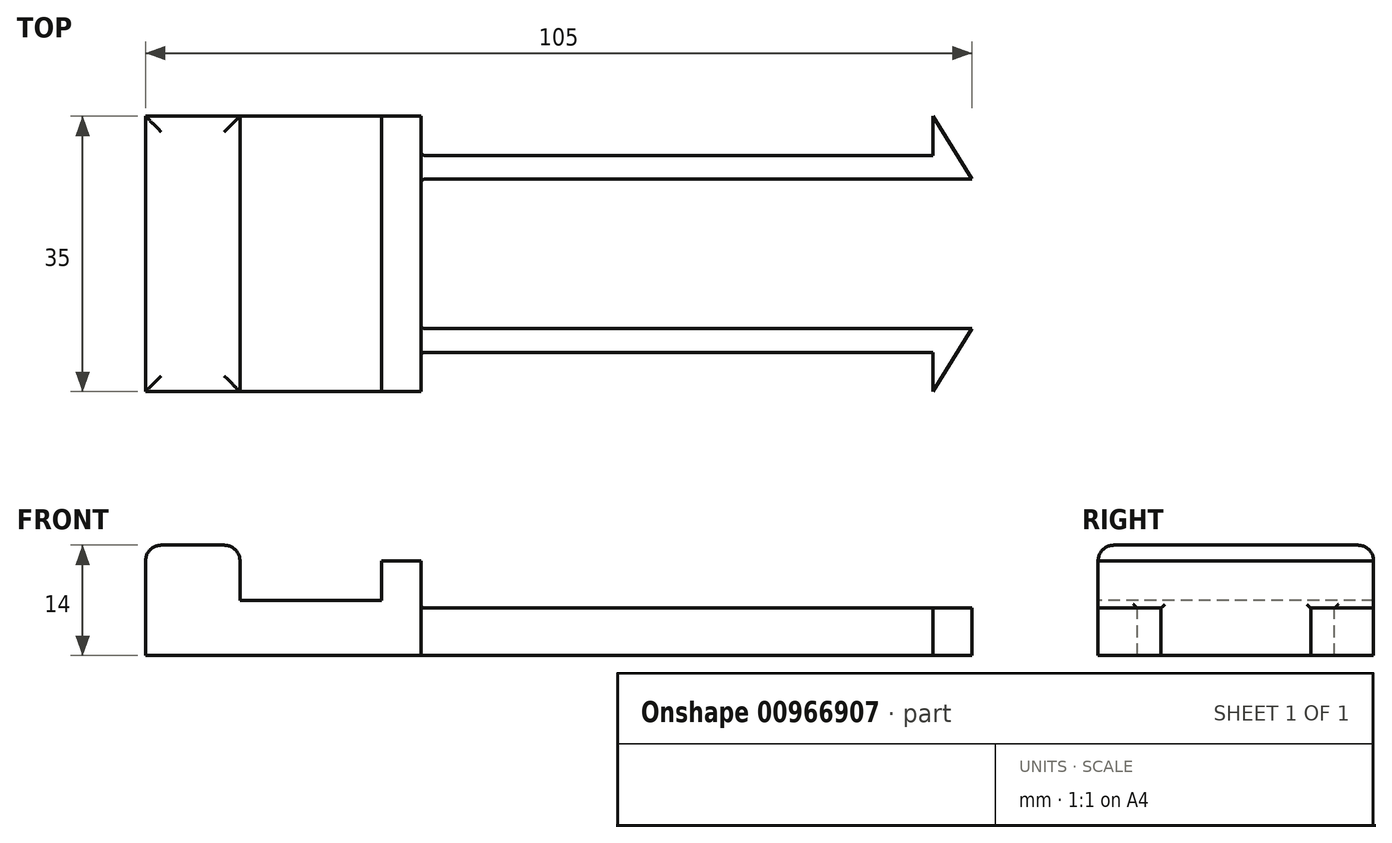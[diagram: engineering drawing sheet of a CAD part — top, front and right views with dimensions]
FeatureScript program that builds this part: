
annotation { "Feature Type Name" : "Feature", "Feature Type Description" : "" }
export const myFeature = defineFeature(function(context is Context, id is Id, definition is map)
    precondition{}
    {
        {
            var Q0;
            Q0=qCreatedBy(makeId("Top.planeOp"),FACE);
            var sketch = newSketch(context, id + "F0", { "sketchPlane" : qUnion([Q0])});
            skLineSegment(sketch, "E0.bottom", {"start": v(52.5, -17.5) * mm, "end": v(-52.5, -17.5) * mm});
            skLineSegment(sketch, "E0.top", {"start": v(52.5, 17.5) * mm, "end": v(-52.5, 17.5) * mm});
            skLineSegment(sketch, "E0.left", {"start": v(52.5, -17.5) * mm, "end": v(52.5, 17.5) * mm});
            skLineSegment(sketch, "E0.right", {"start": v(-52.5, -17.5) * mm, "end": v(-52.5, 17.5) * mm});
            skPoint(sketch, "E0.middle", {"position": v(0, 0) * mm});
            skSolve(sketch);
        }
        {
            var Q0;
            Q0 = qSketchRegion(id + "F0", true);
            extrude(context, id + "F1", {"entities" : qUnion([Q0]), "depth" : 7 * mm, "offsetDistance" : 25 * mm});
        }
        {
            var Q0;
            Q0=makeQuery(id+"F1.opExtrude","CAP_FACE",FACE,{"disambiguationData":[OSD([sQuery(id+"F0.wireOp",EDGE,"E0.bottom"),sQuery(id+"F0.wireOp",EDGE,"E0.top"),sQuery(id+"F0.wireOp",EDGE,"E0.left"),sQuery(id+"F0.wireOp",EDGE,"E0.right")])],"isStart":false});
            var sketch = newSketch(context, id + "F2", { "sketchPlane" : qUnion([Q0])});
            skLineSegment(sketch, "E1", {"start": v(-17.5, 17.5) * mm, "end": v(-17.5, -17.5) * mm});
            skLineSegment(sketch, "E2", {"start": v(-17.5, 9.5) * mm, "end": v(52.5, 9.5) * mm});
            skLineSegment(sketch, "E3", {"start": v(-17.5, -9.5) * mm, "end": v(52.5, -9.5) * mm});
            skSolve(sketch);
        }
        {
            var Q0;
            Q0 = qSketchRegion(id + "F2", true);
            var Q1;
            {var subQ0=sQuery(id+"F2.wireOp",EDGE,"E2");Q1=makeQuery(id+"F2.imprint","IMPRINT",FACE,{"disambiguationData":[TD([[makeQuery(id+"F2.imprint","IMPRINT",EDGE,{"derivedFrom":subQ0}),-1.0]])]});}
            extrude(context, id + "F3", {"entities" : qUnion([Q0, Q1]), "operationType" : NewBodyOperationType.REMOVE, "endBound" : BoundingType.THROUGH_ALL, "oppositeDirection" : true, "depth" : 25 * mm, "offsetDistance" : 25 * mm});
        }
        {
            var Q0;
            Q0=makeQuery(id+"F1.opExtrude","CAP_FACE",FACE,{"disambiguationData":[OSD([sQuery(id+"F0.wireOp",EDGE,"E0.bottom"),sQuery(id+"F0.wireOp",EDGE,"E0.top"),sQuery(id+"F0.wireOp",EDGE,"E0.left"),sQuery(id+"F0.wireOp",EDGE,"E0.right")])],"isStart":false});
            var sketch = newSketch(context, id + "F4", { "sketchPlane" : qUnion([Q0])});
            skLineSegment(sketch, "E4", {"start": v(47.5, 17.5) * mm, "end": v(47.5, -17.5) * mm, "construction": true});
            skLineSegment(sketch, "E5", {"start": v(47.5, 17.5) * mm, "end": v(52.5, 9.5) * mm});
            skSolve(sketch);
        }
        {
            var Q0;
            Q0 = qSketchRegion(id + "F4", true);
            var Q1;
            {var subQ0=sQuery(id+"F4.wireOp",EDGE,"E5");Q1=makeQuery(id+"F4.imprint","IMPRINT",FACE,{"disambiguationData":[TD([[makeQuery(id+"F4.imprint","IMPRINT",EDGE,{"derivedFrom":subQ0}),1.0]])]});}
            extrude(context, id + "F5", {"entities" : qUnion([Q0, Q1]), "operationType" : NewBodyOperationType.REMOVE, "endBound" : BoundingType.THROUGH_ALL, "oppositeDirection" : true, "depth" : 25 * mm, "offsetDistance" : 25 * mm});
        }
        {
            var Q0;
            Q0=makeQuery(id+"F1.opExtrude","CAP_FACE",FACE,{"disambiguationData":[OSD([sQuery(id+"F0.wireOp",EDGE,"E0.bottom"),sQuery(id+"F0.wireOp",EDGE,"E0.top"),sQuery(id+"F0.wireOp",EDGE,"E0.left"),sQuery(id+"F0.wireOp",EDGE,"E0.right")])],"isStart":false});
            var sketch = newSketch(context, id + "F6", { "sketchPlane" : qUnion([Q0])});
            skLineSegment(sketch, "E6", {"start": v(47.5, -9.5) * mm, "end": v(47.5, -17.5) * mm});
            skLineSegment(sketch, "E7", {"start": v(47.5, -17.5) * mm, "end": v(52.5, -9.5) * mm});
            skSolve(sketch);
        }
        {
            var Q0;
            Q0 = qSketchRegion(id + "F6", true);
            var Q1;
            {var subQ0=sQuery(id+"F6.wireOp",EDGE,"E7");Q1=makeQuery(id+"F6.imprint","IMPRINT",FACE,{"disambiguationData":[TD([[makeQuery(id+"F6.imprint","IMPRINT",EDGE,{"derivedFrom":subQ0}),-1.0]])]});}
            extrude(context, id + "F7", {"entities" : qUnion([Q0, Q1]), "operationType" : NewBodyOperationType.REMOVE, "endBound" : BoundingType.THROUGH_ALL, "oppositeDirection" : true, "depth" : 25 * mm, "offsetDistance" : 25 * mm});
        }
        {
            var Q0;
            Q0=makeQuery(id+"F1.opExtrude","CAP_FACE",FACE,{"disambiguationData":[OSD([sQuery(id+"F0.wireOp",EDGE,"E0.bottom"),sQuery(id+"F0.wireOp",EDGE,"E0.top"),sQuery(id+"F0.wireOp",EDGE,"E0.left"),sQuery(id+"F0.wireOp",EDGE,"E0.right")])],"isStart":false});
            var sketch = newSketch(context, id + "F8", { "sketchPlane" : qUnion([Q0])});
            skLineSegment(sketch, "E8", {"start": v(-17.5, 17.5) * mm, "end": v(-17.5, -17.5) * mm, "construction": true});
            skLineSegment(sketch, "E9.bottom", {"start": v(-17.5, 17.5) * mm, "end": v(47.5, 17.5) * mm});
            skLineSegment(sketch, "E9.top", {"start": v(-17.5, 12.5) * mm, "end": v(47.5, 12.5) * mm});
            skLineSegment(sketch, "E9.left", {"start": v(-17.5, 17.5) * mm, "end": v(-17.5, 12.5) * mm});
            skLineSegment(sketch, "E9.right", {"start": v(47.5, 17.5) * mm, "end": v(47.5, 12.5) * mm});
            skSolve(sketch);
        }
        {
            var Q0;
            Q0 = qSketchRegion(id + "F8", true);
            extrude(context, id + "F9", {"entities" : qUnion([Q0]), "operationType" : NewBodyOperationType.REMOVE, "endBound" : BoundingType.THROUGH_ALL, "oppositeDirection" : true, "depth" : 25 * mm, "offsetDistance" : 25 * mm});
        }
        {
            var Q0;
            Q0=makeQuery(id+"F1.opExtrude","CAP_FACE",FACE,{"disambiguationData":[OSD([sQuery(id+"F0.wireOp",EDGE,"E0.bottom"),sQuery(id+"F0.wireOp",EDGE,"E0.top"),sQuery(id+"F0.wireOp",EDGE,"E0.left"),sQuery(id+"F0.wireOp",EDGE,"E0.right")])],"isStart":false});
            var sketch = newSketch(context, id + "F10", { "sketchPlane" : qUnion([Q0])});
            skLineSegment(sketch, "E10", {"start": v(-17.5, 17.5) * mm, "end": v(-17.5, -17.5) * mm, "construction": true});
            skLineSegment(sketch, "E11.bottom", {"start": v(-17.5, -17.5) * mm, "end": v(47.5, -17.5) * mm});
            skLineSegment(sketch, "E11.top", {"start": v(-17.5, -12.5) * mm, "end": v(47.5, -12.5) * mm});
            skLineSegment(sketch, "E11.left", {"start": v(-17.5, -17.5) * mm, "end": v(-17.5, -12.5) * mm});
            skLineSegment(sketch, "E11.right", {"start": v(47.5, -17.5) * mm, "end": v(47.5, -12.5) * mm});
            skSolve(sketch);
        }
        {
            var Q0;
            Q0 = qSketchRegion(id + "F10", true);
            extrude(context, id + "F11", {"entities" : qUnion([Q0]), "operationType" : NewBodyOperationType.REMOVE, "endBound" : BoundingType.THROUGH_ALL, "oppositeDirection" : true, "depth" : 25 * mm, "offsetDistance" : 25 * mm});
        }
        {
            var Q0;
            Q0=makeQuery(id+"F1.opExtrude","CAP_FACE",FACE,{"disambiguationData":[OSD([sQuery(id+"F0.wireOp",EDGE,"E0.bottom"),sQuery(id+"F0.wireOp",EDGE,"E0.top"),sQuery(id+"F0.wireOp",EDGE,"E0.left"),sQuery(id+"F0.wireOp",EDGE,"E0.right")])],"isStart":false});
            var sketch = newSketch(context, id + "F12", { "sketchPlane" : qUnion([Q0])});
            skPoint(sketch, "E12", {"position": v(-22.5, 17.5) * mm});
            skLineSegment(sketch, "E13.bottom", {"start": v(-22.5, 17.5) * mm, "end": v(-17.5, 17.5) * mm});
            skLineSegment(sketch, "E13.top", {"start": v(-22.5, -17.5) * mm, "end": v(-17.5, -17.5) * mm});
            skLineSegment(sketch, "E13.left", {"start": v(-22.5, 17.5) * mm, "end": v(-22.5, -17.5) * mm});
            skLineSegment(sketch, "E13.right", {"start": v(-17.5, 17.5) * mm, "end": v(-17.5, -17.5) * mm});
            skSolve(sketch);
        }
        {
            var Q0;
            Q0 = qSketchRegion(id + "F12", true);
            extrude(context, id + "F13", {"entities" : qUnion([Q0]), "operationType" : NewBodyOperationType.ADD, "depth" : 5 * mm, "offsetDistance" : 25 * mm});
        }
        {
            var Q0;
            {var subQ0=sQuery(id+"F0.wireOp",EDGE,"E0.top");var subQ1=sQuery(id+"F0.wireOp",EDGE,"E0.right");var subQ2=sQuery(id+"F0.wireOp",EDGE,"E0.bottom");Q0=makeQuery(id+"F13.boolean.opBoolean","SPLIT",FACE,{"disambiguationData":[TD([makeQuery(id+"F1.opExtrude","SWEPT_FACE",FACE,{"disambiguationData":[OSD([subQ2])]})])],"derivedFrom":makeQuery(id+"F1.opExtrude","CAP_FACE",FACE,{"disambiguationData":[OSD([subQ2,subQ0,sQuery(id+"F0.wireOp",EDGE,"E0.left"),subQ1])],"isStart":false})});}
            var sketch = newSketch(context, id + "F14", { "sketchPlane" : qUnion([Q0])});
            skLineSegment(sketch, "E14.bottom", {"start": v(-52.5, 17.5) * mm, "end": v(-40.5, 17.5) * mm});
            skLineSegment(sketch, "E14.top", {"start": v(-52.5, -17.5) * mm, "end": v(-40.5, -17.5) * mm});
            skLineSegment(sketch, "E14.left", {"start": v(-52.5, 17.5) * mm, "end": v(-52.5, -17.5) * mm});
            skLineSegment(sketch, "E14.right", {"start": v(-40.5, 17.5) * mm, "end": v(-40.5, -17.5) * mm});
            skSolve(sketch);
        }
        {
            var Q0;
            Q0 = qSketchRegion(id + "F14", true);
            extrude(context, id + "F15", {"entities" : qUnion([Q0]), "operationType" : NewBodyOperationType.ADD, "depth" : 7 * mm, "offsetDistance" : 25 * mm});
        }
        {
            var Q0;
            Q0=makeQuery(id+"F15.opExtrude","CAP_EDGE",EDGE,{"disambiguationData":[OSD([sQuery(id+"F14.wireOp",EDGE,"E14.right")])],"isStart":false});
            var Q1;
            Q1=makeQuery(id+"F15.opExtrude","CAP_EDGE",EDGE,{"disambiguationData":[OSD([sQuery(id+"F14.wireOp",EDGE,"E14.bottom")])],"isStart":false});
            var Q2;
            Q2=makeQuery(id+"F15.opExtrude","CAP_EDGE",EDGE,{"disambiguationData":[OSD([sQuery(id+"F14.wireOp",EDGE,"E14.top")])],"isStart":false});
            var Q3;
            Q3=makeQuery(id+"F15.opExtrude","CAP_EDGE",EDGE,{"disambiguationData":[OSD([sQuery(id+"F14.wireOp",EDGE,"E14.left")])],"isStart":false});
            fillet(context, id + "F16", {"entities" : qUnion([Q0, Q1, Q2, Q3]), "radius" : 2 * mm, "tangentPropagation" : true, "allowEdgeOverflow" : false});
        }
        {
            var Q0;
            Q0=makeQuery(id+"F13.boolean.opBoolean","SPLIT",FACE,{"disambiguationData":[TD([makeQuery(id+"F3.boolean.opBoolean","COPY",FACE,{"derivedFrom":makeQuery(id+"F3.opExtrude","SWEPT_FACE",FACE,{"disambiguationData":[OSD([sQuery(id+"F2.wireOp",EDGE,"E3")])]})})])],"derivedFrom":makeQuery(id+"F1.opExtrude","CAP_FACE",FACE,{"disambiguationData":[OSD([sQuery(id+"F0.wireOp",EDGE,"E0.bottom"),sQuery(id+"F0.wireOp",EDGE,"E0.top"),sQuery(id+"F0.wireOp",EDGE,"E0.left"),sQuery(id+"F0.wireOp",EDGE,"E0.right")])],"isStart":false})});
            var Q1;
            Q1=makeQuery(id+"F13.boolean.opBoolean","SPLIT",FACE,{"disambiguationData":[TD([makeQuery(id+"F3.boolean.opBoolean","COPY",FACE,{"derivedFrom":makeQuery(id+"F3.opExtrude","SWEPT_FACE",FACE,{"disambiguationData":[OSD([sQuery(id+"F2.wireOp",EDGE,"E2")])]})})])],"derivedFrom":makeQuery(id+"F1.opExtrude","CAP_FACE",FACE,{"disambiguationData":[OSD([sQuery(id+"F0.wireOp",EDGE,"E0.bottom"),sQuery(id+"F0.wireOp",EDGE,"E0.top"),sQuery(id+"F0.wireOp",EDGE,"E0.left"),sQuery(id+"F0.wireOp",EDGE,"E0.right")])],"isStart":false})});
            extrude(context, id + "F17", {"entities" : qUnion([Q0, Q1]), "operationType" : NewBodyOperationType.REMOVE, "oppositeDirection" : true, "depth" : 1 * mm, "offsetDistance" : 25 * mm});
        }
        {
            var Q0;
            Q0=makeQuery(id+"F11.boolean.opBoolean","COPY",EDGE,{"derivedFrom":makeQuery(id+"F11.opExtrude","SWEPT_EDGE",EDGE,{"disambiguationData":[OSD([sQuery(id+"F10.wireOp",EDGE,"E11.top"),sQuery(id+"F10.wireOp",EDGE,"E11.left")])]})});
            var Q1;
            {var subQ0=sQuery(id+"F12.wireOp",EDGE,"E13.right");Q1=makeQuery(id+"F17.boolean.opBoolean","COPY",EDGE,{"derivedFrom":makeQuery(id+"F17.opExtrude","CAP_EDGE",EDGE,{"disambiguationData":[OSD([subQ0]),TDD([makeQuery(id+"F13.boolean.opBoolean","SPLIT",EDGE,{"disambiguationData":[TD([makeQuery(id+"F3.boolean.opBoolean","COPY",FACE,{"derivedFrom":makeQuery(id+"F3.opExtrude","SWEPT_FACE",FACE,{"disambiguationData":[OSD([sQuery(id+"F2.wireOp",EDGE,"E3")])]})})])],"derivedFrom":makeQuery(id+"F13.opExtrude","CAP_EDGE",EDGE,{"disambiguationData":[OSD([subQ0])],"isStart":true})})])],"isStart":false})});}
            var Q2;
            Q2=makeQuery(id+"F3.boolean.opBoolean","COPY",EDGE,{"derivedFrom":makeQuery(id+"F3.opExtrude","SWEPT_EDGE",EDGE,{"disambiguationData":[OSD([sQuery(id+"F2.wireOp",EDGE,"E1"),sQuery(id+"F2.wireOp",EDGE,"E2")])]})});
            var Q3;
            {var subQ0=sQuery(id+"F12.wireOp",EDGE,"E13.right");Q3=makeQuery(id+"F17.boolean.opBoolean","COPY",EDGE,{"derivedFrom":makeQuery(id+"F17.opExtrude","CAP_EDGE",EDGE,{"disambiguationData":[OSD([subQ0]),TDD([makeQuery(id+"F13.boolean.opBoolean","SPLIT",EDGE,{"disambiguationData":[TD([makeQuery(id+"F3.boolean.opBoolean","COPY",FACE,{"derivedFrom":makeQuery(id+"F3.opExtrude","SWEPT_FACE",FACE,{"disambiguationData":[OSD([sQuery(id+"F2.wireOp",EDGE,"E2")])]})})])],"derivedFrom":makeQuery(id+"F13.opExtrude","CAP_EDGE",EDGE,{"disambiguationData":[OSD([subQ0])],"isStart":true})})])],"isStart":false})});}
            var Q4;
            Q4=makeQuery(id+"F3.boolean.opBoolean","COPY",EDGE,{"derivedFrom":makeQuery(id+"F3.opExtrude","SWEPT_EDGE",EDGE,{"disambiguationData":[OSD([sQuery(id+"F2.wireOp",EDGE,"E1"),sQuery(id+"F2.wireOp",EDGE,"E3")])]})});
            var Q5;
            Q5=makeQuery(id+"F9.boolean.opBoolean","COPY",EDGE,{"derivedFrom":makeQuery(id+"F9.opExtrude","SWEPT_EDGE",EDGE,{"disambiguationData":[OSD([sQuery(id+"F8.wireOp",EDGE,"E9.top"),sQuery(id+"F8.wireOp",EDGE,"E9.left")])]})});
            fillet(context, id + "F18", {"entities" : qUnion([Q0, Q1, Q2, Q3, Q4, Q5]), "radius" : .5 * mm, "tangentPropagation" : true, "allowEdgeOverflow" : false});
        }
    });
